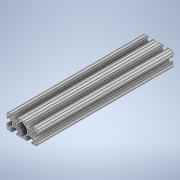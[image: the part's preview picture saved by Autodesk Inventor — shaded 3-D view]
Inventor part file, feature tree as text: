
AUTODESK INVENTOR PART (.ipt)
format: ipt  version: 2020 (Build 240168000, 168)  size: 334,336 bytes
history: native  units: in
note: dims shown in document units (in); Inventor stores cm internally (conversion verified against a paired STEP export)
features: sketch x2, extrude x1
ambient origin geometry x8: Origin, YZ Plane, XZ Plane, XY Plane, X Axis, Y Axis, Z Axis, Center Point
bodies: Solid1 (feature_tree)
feature tree (3):
  extrude  "Extrusion1"  [1 undecoded]
  sketch  "Sketch2"
  sketch  "Sketch1"  dims[d0=9.0in d1=0.0in]
note: 1 required parameter value undecoded (feature->parameter linkage not recoverable at this tier; creation-order binding heuristic only, values carry confidence <= 0.55)
